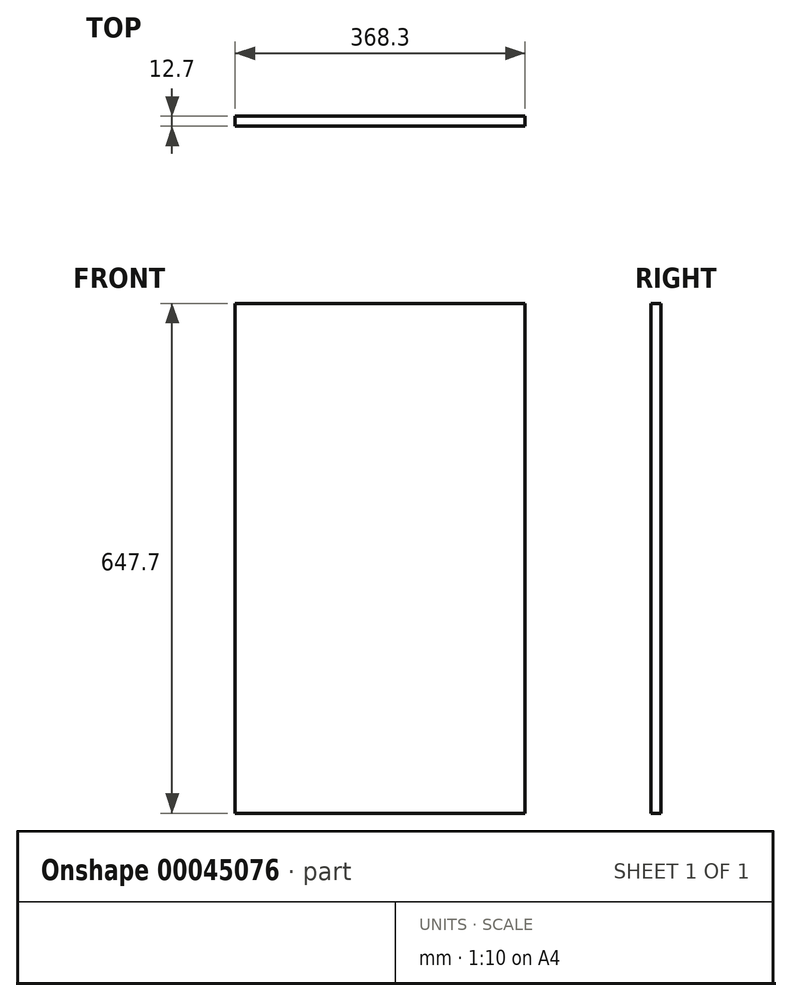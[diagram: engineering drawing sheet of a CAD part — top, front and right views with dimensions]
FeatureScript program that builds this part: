
annotation { "Feature Type Name" : "Feature", "Feature Type Description" : "" }
export const myFeature = defineFeature(function(context is Context, id is Id, definition is map)
    precondition{}
    {
        {
            var Q0;
            Q0=qCreatedBy(makeId("Front.planeOp"),FACE);
            var sketch = newSketch(context, id + "F0", { "sketchPlane" : qUnion([Q0])});
            skLineSegment(sketch, "E0.bottom", {"start": v(-35.28, 588.3) * mm, "end": v(333.02, 588.3) * mm});
            skLineSegment(sketch, "E0.top", {"start": v(-35.28, -59.4) * mm, "end": v(333.02, -59.4) * mm});
            skLineSegment(sketch, "E0.left", {"start": v(-35.28, 588.3) * mm, "end": v(-35.28, -59.4) * mm});
            skLineSegment(sketch, "E0.right", {"start": v(333.02, 588.3) * mm, "end": v(333.02, -59.4) * mm});
            skSolve(sketch);
        }
        {
            var Q0;
            Q0=makeQuery(id+"F0.imprint","IMPRINT",FACE,{"disambiguationData":[TD([[makeQuery(id+"F0.imprint","IMPRINT",EDGE,{"derivedFrom":sQuery(id+"F0.wireOp",EDGE,"E0.bottom")}),-1.0]])]});
            extrude(context, id + "F1", {"entities" : qUnion([Q0]), "depth" : 12.7 * mm});
        }
    });
